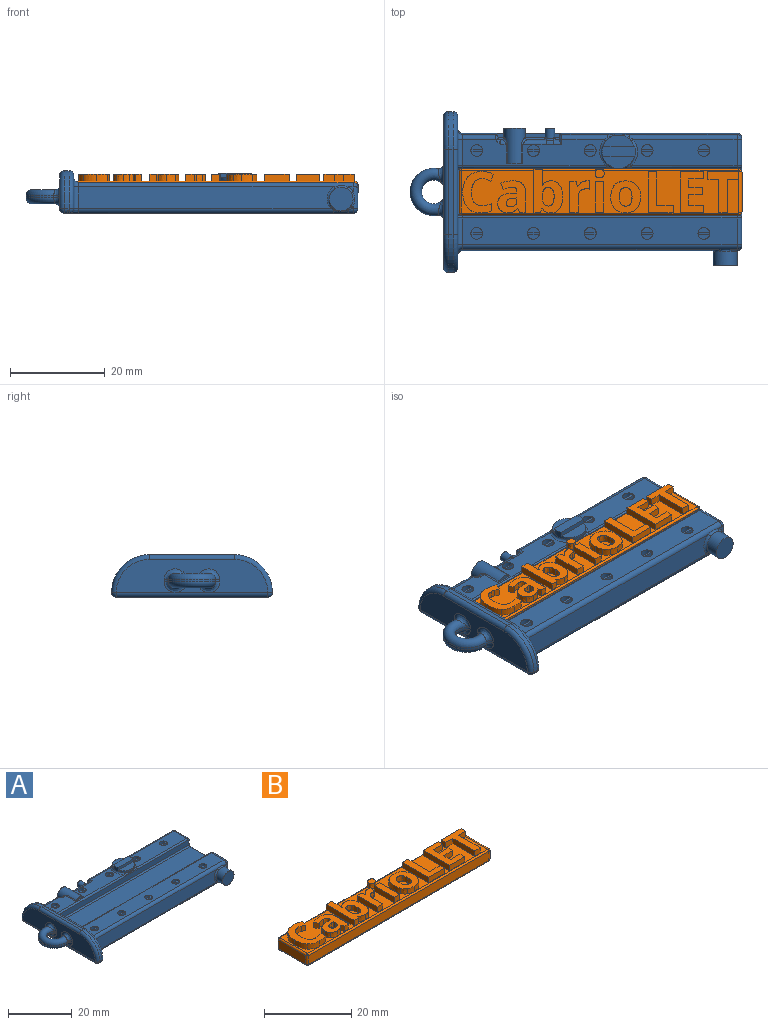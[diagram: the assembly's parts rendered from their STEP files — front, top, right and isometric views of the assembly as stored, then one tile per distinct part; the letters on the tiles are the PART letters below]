
ASSEMBLY  parts=2 mates=1
PART A: 212 faces, bbox 70.7x35.5x9.8 mm
  f0: plane 54.03x4.5mm, normal (0,-1,0.08), area 238.5mm2, adj f1,f2,f3,f4
  f1: cylinder r=1mm len=53.9mm, axis (-1,0,0), area 88.6mm2, adj f0,f5,f6,f7,f8
  f2: bspline ~4.5x1.77mm, area 3.6mm2, adj f0,f6,f9,f10
  f3: cylinder r=1mm len=58mm, axis (1,0,0), area 86.1mm2, adj f0,f9,f11,f12,f13,f14
  f4: cylinder r=1mm len=4.73mm, axis (0,-0.08,-1), area 7.2mm2, adj f0,f7,f14,f15
  f5: bspline ~3.53x1.2mm, area 2.9mm2, adj f1,f8,f16,f17
  f6: bspline ~1.72x1.23mm, area 0.5mm2, adj f1,f2,f10,f17
  f7: bspline ~2.35x2.35mm, area 3.4mm2, adj f1,f4,f8,f18
  f8: plane 61x32mm, normal (0,0,-1), area 1404.4mm2, adj f1,f5,f7,f16,f18,f19,f20,f21
  f9: bspline ~3.78x0.89mm, area 1.8mm2, adj f2,f3,f10,f26
  f10: cylinder r=2.5mm len=5mm, axis (0,1,0), area 43.4mm2, adj f2,f6,f9,f17,f26,f27,f28,f29
  f11: plane 1.03x0.96mm, normal (0,-1,0.08), area 0.4mm2, adj f3,f26,f31
  f12: sphere r=1mm, area 1.5mm2, adj f3,f31,f32
  f13: plane 58x5.57mm, normal (0,0,1), area 298.7mm2, adj f3,f32,f33,f34,f35,f36,f37,f38
  f14: torus R=2mm, axis (1,0,0), area 3.2mm2, adj f3,f4,f15,f39
  f15: plane 32.15x7.15mm, normal (1,0,0), area 68.5mm2, adj f4,f14,f18,f22,f39,f40,f41,f42
  f16: cylinder r=1mm len=1.08mm, axis (-1,0,0), area 1.3mm2, adj f5,f8,f29,f51,f52
  f17: bspline ~3.57x0.73mm, area -0.2mm2, adj f5,f6,f10,f29
  f18: cylinder r=1mm len=2.57mm, axis (0,1,0), area 4mm2, adj f7,f8,f15,f53
  f19: cylinder r=1mm len=1mm, axis (1,0,0), area 1.6mm2, adj f8,f53,f54,f55
  f20: cylinder r=1mm len=32mm, axis (0,-1,0), area 50.3mm2, adj f8,f54,f56,f57
  f21: cylinder r=1mm len=1mm, axis (-1,0,0), area 1.6mm2, adj f8,f56,f58,f59
  f22: cylinder r=1mm len=2.57mm, axis (0,1,0), area 4mm2, adj f8,f15,f23,f59
  f23: bspline ~2.35x2.09mm, area 3.4mm2, adj f8,f22,f24,f46
  f24: cylinder r=1mm len=58mm, axis (1,0,0), area 94.5mm2, adj f8,f23,f60,f61,f62,f63,f64,f65
  f25: cylinder r=1mm len=22.84mm, axis (0,1,0), area 35.9mm2, adj f8,f52,f63,f66
  f26: bspline ~1.28x1.19mm, area 1mm2, adj f9,f10,f11,f27
  f27: bspline ~4.11x1.01mm, area 2.1mm2, adj f10,f26,f30,f31
  f28: plane 5x5mm, normal (0,-1,0), area 19.6mm2, adj f10
  f29: bspline ~1.72x1.23mm, area 0.6mm2, adj f10,f16,f17,f30
  f30: bspline ~0.56x0.54mm, area 0.2mm2, adj f10,f27,f29,f51
  f31: cylinder r=1mm len=4.58mm, axis (0,-0.08,-1), area 6.3mm2, adj f11,f12,f27,f51,f52,f66
  f32: cylinder r=1mm len=5.57mm, axis (0,-1,0), area 8.8mm2, adj f12,f13,f66,f67
  f33: cylinder r=1.25mm len=2.5mm, axis (0,0,1), area 10.5mm2, adj f13,f68,f69,f70,f71,f72
  f34: cylinder r=1.25mm len=2.5mm, axis (0,0,1), area 10.5mm2, adj f13,f73,f74,f75,f76,f77
  f35: cylinder r=1.25mm len=2.5mm, axis (0,0,1), area 10.5mm2, adj f13,f78,f79,f80,f81,f82
  f36: cylinder r=1.25mm len=2.5mm, axis (0,0,1), area 10.5mm2, adj f13,f83,f84,f85,f86,f87
  f37: cylinder r=1.25mm len=2.5mm, axis (0,0,1), area 10.5mm2, adj f13,f88,f89,f90,f91,f92
  f38: cylinder r=0.5mm len=58mm, axis (-1,0,0), area 45.6mm2, adj f13,f40,f50,f67
  f39: cylinder r=1mm len=5.57mm, axis (0,1,0), area 8.8mm2, adj f13,f14,f15,f50
  f40: plane 59.5x2.38mm, normal (0,1,0), area 119.1mm2, adj f15,f38,f50,f67,f93,f94
  f41: cylinder r=0.5mm len=10mm, axis (0,1,0), area 7.5mm2, adj f15,f94,f95,f96
  f42: plane 59.5x2.38mm, normal (0,-1,0), area 119.1mm2, adj f15,f43,f95,f97,f98,f99,f100,f101
  f43: torus R=1.5mm, axis (0,-1,0), area 1mm2, adj f15,f42,f44,f97
  f44: cylinder r=1mm len=5.57mm, axis (0,1,0), area 8.8mm2, adj f15,f43,f45,f103
  f45: torus R=2mm, axis (1,0,0), area 3.2mm2, adj f15,f44,f46,f104
  f46: cylinder r=1mm len=4.73mm, axis (0,0.08,-1), area 7.2mm2, adj f15,f23,f45,f64
  f47: torus R=7mm, axis (1,0,0), area 18.8mm2, adj f15,f48,f58,f59
  f48: cylinder r=1mm len=18mm, axis (0,-1,0), area 28.3mm2, adj f15,f47,f49,f105
  f49: torus R=7mm, axis (1,0,0), area 18.8mm2, adj f15,f48,f53,f55
  f50: torus R=1.5mm, axis (0,-1,0), area 1mm2, adj f15,f38,f39,f40
  f51: plane 0.23x0.17mm, normal (0,-1,0.08), area 0mm2, adj f16,f30,f31
  f52: sphere r=1mm, area 1.6mm2, adj f16,f25,f31
  f53: sphere r=1mm, area 2.1mm2, adj f18,f19,f49
  f54: sphere r=1mm, area 1.6mm2, adj f19,f20,f106
  f55: cylinder r=8mm len=8mm, axis (-1,0,0), area 12.6mm2, adj f19,f49,f105,f106
  f56: sphere r=1mm, area 2.1mm2, adj f20,f21,f107
  f57: plane 32x7mm, normal (-1,0,0), area 203mm2, adj f20,f106,f107,f108
  f58: cylinder r=8mm len=8mm, axis (1,0,0), area 12.6mm2, adj f21,f47,f105,f107
  f59: sphere r=1mm, area 1mm2, adj f21,f22,f47
  f60: plane 14x0.92mm, normal (0,0,1), area 12.1mm2, adj f24,f61,f65,f109,f110,f111
  f61: torus R=0.5mm, axis (1,0,0), area 0mm2, adj f24,f60,f111,f112
  f62: plane 37x5.41mm, normal (0,1,0.08), area 168.6mm2, adj f24,f112,f113,f114,f115,f116,f117,f118
  f63: sphere r=1mm, area 1mm2, adj f24,f25,f114
  f64: plane 7x4.5mm, normal (0,1,0.08), area 31.6mm2, adj f24,f46,f104,f119
  f65: torus R=0.5mm, axis (1,0,0), area 0mm2, adj f24,f60,f109,f119
  f66: plane 22.84x4.5mm, normal (1,0,0), area 74.2mm2, adj f25,f31,f32,f93,f98,f114,f120,f121
  f67: torus R=0.5mm, axis (0,-1,0), area 1mm2, adj f32,f38,f40,f93
  f68: plane 2.5x0.5mm, normal (0,0,1), area 1.2mm2, adj f33,f69,f71
  f69: plane 2.45x1.3mm, normal (0,1,0), area 3.2mm2, adj f33,f68,f70
  f70: plane 2.45x1mm, normal (0,0,1), area 1.8mm2, adj f33,f69
  f71: plane 2.45x1.3mm, normal (0,-1,0), area 3.2mm2, adj f33,f68,f72
  f72: plane 2.45x1mm, normal (0,0,1), area 1.8mm2, adj f33,f71
  f73: plane 2.5x0.5mm, normal (0,0,1), area 1.2mm2, adj f34,f74,f76
  f74: plane 2.45x1.3mm, normal (0,1,0), area 3.2mm2, adj f34,f73,f75
  f75: plane 2.45x1mm, normal (0,0,1), area 1.8mm2, adj f34,f74
  f76: plane 2.45x1.3mm, normal (0,-1,0), area 3.2mm2, adj f34,f73,f77
  f77: plane 2.45x1mm, normal (0,0,1), area 1.8mm2, adj f34,f76
  f78: plane 2.5x0.5mm, normal (0,0,1), area 1.2mm2, adj f35,f79,f81
  f79: plane 2.45x1.3mm, normal (0,1,0), area 3.2mm2, adj f35,f78,f80
  f80: plane 2.45x1mm, normal (0,0,1), area 1.8mm2, adj f35,f79
  f81: plane 2.45x1.3mm, normal (0,-1,0), area 3.2mm2, adj f35,f78,f82
  f82: plane 2.45x1mm, normal (0,0,1), area 1.8mm2, adj f35,f81
  f83: plane 2.5x0.5mm, normal (0,0,1), area 1.2mm2, adj f36,f84,f86
  f84: plane 2.45x1.3mm, normal (0,1,0), area 3.2mm2, adj f36,f83,f85
  f85: plane 2.45x1mm, normal (0,0,1), area 1.8mm2, adj f36,f84
  f86: plane 2.45x1.3mm, normal (0,-1,0), area 3.2mm2, adj f36,f83,f87
  f87: plane 2.45x1mm, normal (0,0,1), area 1.8mm2, adj f36,f86
  f88: plane 2.5x0.5mm, normal (0,0,1), area 1.2mm2, adj f37,f89,f91
  f89: plane 2.45x1.3mm, normal (0,1,0), area 3.2mm2, adj f37,f88,f90
  f90: plane 2.45x1mm, normal (0,0,1), area 1.8mm2, adj f37,f89
  f91: plane 2.45x1.3mm, normal (0,-1,0), area 3.2mm2, adj f37,f88,f92
  f92: plane 2.45x1mm, normal (0,0,1), area 1.8mm2, adj f37,f91
  f93: cylinder r=0.5mm len=1.5mm, axis (0,0,-1), area 1.2mm2, adj f40,f66,f67,f120
  f94: cylinder r=0.5mm len=59.5mm, axis (1,0,0), area 46.5mm2, adj f40,f41,f96,f120
  f95: cylinder r=0.5mm len=59.5mm, axis (-1,0,0), area 46.5mm2, adj f41,f42,f96,f122
  f96: plane 59x9mm, normal (0,0,1), area 531mm2, adj f41,f94,f95,f123
  f97: cylinder r=0.5mm len=30.4mm, axis (1,0,0), area 23.9mm2, adj f42,f43,f102,f103,f124
  f98: cylinder r=0.5mm len=1.5mm, axis (0,0,1), area 1.2mm2, adj f42,f66,f99,f122
  f99: torus R=0.5mm, axis (0,-1,0), area 1mm2, adj f42,f98,f100,f121
  f100: cylinder r=0.5mm len=22.4mm, axis (1,0,0), area 17.6mm2, adj f42,f99,f101,f125,f126
  f101: bspline ~2.65x0.51mm, area 1.1mm2, adj f42,f100,f102,f126
  f102: bspline ~2.65x0.51mm, area 1.1mm2, adj f42,f97,f101,f124
  f103: plane 30.35x5.58mm, normal (0,0,1), area 120.2mm2, adj f44,f97,f104,f113,f127,f128,f129,f130
  f104: cylinder r=1mm len=7.05mm, axis (1,0,0), area 10.5mm2, adj f45,f64,f103,f140,f141
  f105: plane 18x1mm, normal (0,0,1), area 18mm2, adj f48,f55,f58,f108
  f106: torus R=7mm, axis (-1,0,0), area 18.8mm2, adj f54,f55,f57,f108
  f107: torus R=7mm, axis (-1,0,0), area 18.8mm2, adj f56,f57,f58,f108
  f108: cylinder r=1mm len=18mm, axis (0,1,0), area 28.3mm2, adj f57,f105,f106,f107
  f109: plane 4.81x0.45mm, normal (1,0,0), area 1.1mm2, adj f60,f65,f119,f141,f142,f143
  f110: cylinder r=0.5mm len=13mm, axis (-1,0,0), area 10mm2, adj f60,f111,f143,f144
  f111: plane 5x1.05mm, normal (-1,0,0), area 3.6mm2, adj f60,f61,f110,f112,f135,f136,f144,f145
  f112: cylinder r=0.5mm len=4.54mm, axis (0,0.08,-1), area 3.5mm2, adj f61,f62,f111,f145
  f113: cylinder r=1mm len=9.63mm, axis (1,0,0), area 14.2mm2, adj f62,f103,f118,f145,f146
  f114: cylinder r=1mm len=4.58mm, axis (0,0.08,-1), area 7.1mm2, adj f62,f63,f66,f147
  f115: cylinder r=1mm len=22.63mm, axis (1,0,0), area 33.7mm2, adj f62,f116,f125,f147,f148
  f116: bspline ~2.69x1.16mm, area 0.8mm2, adj f62,f115,f149
  f117: bspline ~0.06x0.04mm, area 0mm2, adj f62,f149,f150,f151
  f118: bspline ~2.69x1.16mm, area 0.8mm2, adj f62,f113,f150
  f119: cylinder r=0.5mm len=4.54mm, axis (0,0.08,-1), area 3.5mm2, adj f64,f65,f109,f141
  f120: torus R=1mm, axis (1,0,0), area 0.8mm2, adj f66,f93,f94,f123
  f121: cylinder r=1mm len=5.57mm, axis (0,-1,0), area 8.8mm2, adj f66,f99,f125,f147
  f122: torus R=1mm, axis (1,0,0), area 0.8mm2, adj f66,f95,f98,f123
  f123: cylinder r=0.5mm len=9mm, axis (0,-1,0), area 7.1mm2, adj f66,f96,f120,f122
  f124: bspline ~2.65x0.73mm, area 0.8mm2, adj f97,f102,f134,f152
  f125: plane 22.35x5.57mm, normal (0,0,1), area 109.2mm2, adj f100,f115,f121,f153,f154,f155
  f126: bspline ~2.65x0.73mm, area 0.8mm2, adj f100,f101,f155,f156
  f127: cylinder r=1.25mm len=2.5mm, axis (0,0,1), area 10.5mm2, adj f103,f157,f158,f159,f160,f161
  f128: cylinder r=1mm len=4.92mm, axis (1,0,0), area 6.9mm2, adj f103,f137,f144,f162,f163
  f129: cylinder r=0.5mm len=4mm, axis (0,-1,0), area 1.4mm2, adj f103,f130,f162,f164
  f130: plane 3.55x0.65mm, normal (0,-1,0), area 1.4mm2, adj f103,f129,f131,f164
  f131: cylinder r=0.5mm len=4mm, axis (0,-1,0), area 1.4mm2, adj f103,f130,f164,f165
  f132: cylinder r=1mm len=1.22mm, axis (1,0,0), area 1.2mm2, adj f103,f142,f144,f165
  f133: bspline ~1.37x1mm, area 0.3mm2, adj f103,f140,f142
  f134: torus R=4mm, axis (0,0,1), area 4.5mm2, adj f103,f124,f146,f151,f152
  f135: cylinder r=0.5mm len=1.07mm, axis (0,-1,0), area 0.5mm2, adj f103,f111,f136,f145
  f136: cylinder r=1mm len=1.7mm, axis (1,0,0), area 2mm2, adj f103,f111,f135,f137,f144,f166
  f137: bspline ~2.14x1.15mm, area 1.5mm2, adj f103,f128,f136,f167
  f138: cylinder r=1.25mm len=2.5mm, axis (0,0,1), area 10.5mm2, adj f103,f168,f169,f170,f171,f172
  f139: cylinder r=1.25mm len=2.5mm, axis (0,0,1), area 10.5mm2, adj f103,f173,f174,f175,f176,f177
  f140: bspline ~0.96x0.8mm, area 0.5mm2, adj f104,f133,f141,f142
  f141: torus R=0.5mm, axis (1,0,0), area 0.4mm2, adj f104,f109,f119,f140
  f142: torus R=1.5mm, axis (1,0,0), area 0.7mm2, adj f109,f132,f133,f140,f143
  f143: cylinder r=0.5mm len=4.5mm, axis (0,0,1), area 3.3mm2, adj f109,f110,f142,f144
  f144: plane 12.5x4mm, normal (0,1,0), area 29.6mm2, adj f110,f111,f128,f132,f136,f143,f178,f179
  f145: torus R=0.5mm, axis (1,0,0), area 1mm2, adj f111,f112,f113,f135
  f146: bspline ~1.65x1.1mm, area 0.6mm2, adj f113,f134,f150,f151
  f147: sphere r=1mm, area 1mm2, adj f114,f115,f121
  f148: bspline ~1.83x1.31mm, area 0.6mm2, adj f115,f149,f151,f155
  f149: bspline ~2.44x0.79mm, area 0.7mm2, adj f116,f117,f148,f151
  f150: bspline ~2.4x0.76mm, area 0.7mm2, adj f117,f118,f146,f151
  f151: cylinder r=3.5mm len=7mm, axis (0,0,-1), area 16.7mm2, adj f117,f134,f146,f148,f149,f150,f152,f155
  f152: bspline ~2.38x0.88mm, area 0.9mm2, adj f124,f134,f151,f156
  f153: cylinder r=1.25mm len=2.5mm, axis (0,0,1), area 10.5mm2, adj f125,f185,f186,f187,f188,f189
  f154: cylinder r=1.25mm len=2.5mm, axis (0,0,1), area 10.5mm2, adj f125,f190,f191,f192,f193,f194
  f155: torus R=4mm, axis (0,0,1), area 4.5mm2, adj f125,f126,f148,f151,f156
  f156: bspline ~2.38x0.88mm, area 0.9mm2, adj f126,f151,f152,f155
  f157: plane 2.5x0.5mm, normal (0,0,1), area 1.2mm2, adj f127,f158,f160
  f158: plane 2.45x1.3mm, normal (0,1,0), area 3.2mm2, adj f127,f157,f159
  f159: plane 2.45x1mm, normal (0,0,1), area 1.8mm2, adj f127,f158
  f160: plane 2.45x1.3mm, normal (0,-1,0), area 3.2mm2, adj f127,f157,f161
  f161: plane 2.45x1mm, normal (0,0,1), area 1.8mm2, adj f127,f160
  f162: bspline ~1.57x1.47mm, area 1.1mm2, adj f128,f129,f164,f178
  f163: bspline ~0.97x0.83mm, area 0.4mm2, adj f128,f167,f179,f195
  f164: cylinder r=2.25mm len=7.5mm, axis (0,-1,0), area 47.8mm2, adj f129,f130,f131,f162,f165,f178,f196
  f165: bspline ~1.57x1.47mm, area 1.1mm2, adj f131,f132,f164,f178
  f166: bspline ~1.05x0.78mm, area 0.4mm2, adj f136,f167,f179,f195
  f167: bspline ~1.62x0.46mm, area 0.7mm2, adj f137,f163,f166,f195
  f168: plane 2.45x1.3mm, normal (0,1,0), area 3.2mm2, adj f138,f169,f170
  f169: plane 2.45x1mm, normal (0,0,1), area 1.8mm2, adj f138,f168
  f170: plane 2.5x0.5mm, normal (0,0,1), area 1.2mm2, adj f138,f168,f171
  f171: plane 2.45x1.3mm, normal (0,-1,0), area 3.2mm2, adj f138,f170,f172
  f172: plane 2.45x1mm, normal (0,0,1), area 1.8mm2, adj f138,f171
  f173: plane 2.5x0.5mm, normal (0,0,1), area 1.2mm2, adj f139,f174,f176
  f174: plane 2.45x1.3mm, normal (0,1,0), area 3.2mm2, adj f139,f173,f175
  f175: plane 2.45x1mm, normal (0,0,1), area 1.8mm2, adj f139,f174
  f176: plane 2.45x1.3mm, normal (0,-1,0), area 3.2mm2, adj f139,f173,f177
  f177: plane 2.45x1mm, normal (0,0,1), area 1.8mm2, adj f139,f176
  f178: torus R=2.75mm, axis (0,1,0), area 6.8mm2, adj f144,f162,f164,f165
  f179: torus R=1.5mm, axis (0,1,0), area 3.7mm2, adj f144,f163,f166,f195
  f180: plane 6.71x1mm, normal (0,-1,0), area 6.7mm2, adj f151,f181,f184
  f181: plane 7x2mm, normal (0,0,1), area 13.8mm2, adj f151,f180,f182
  f182: plane 6.71x1mm, normal (0,1,0), area 6.7mm2, adj f151,f181,f183
  f183: plane 6.71x2.5mm, normal (0,0,1), area 12.3mm2, adj f151,f182
  f184: plane 6.71x2.5mm, normal (0,0,1), area 12.3mm2, adj f151,f180
  f185: plane 2.5x0.5mm, normal (0,0,1), area 1.2mm2, adj f153,f186,f188
  f186: plane 2.45x1.3mm, normal (0,1,0), area 3.2mm2, adj f153,f185,f187
  f187: plane 2.45x1mm, normal (0,0,1), area 1.8mm2, adj f153,f186
  f188: plane 2.45x1.3mm, normal (0,-1,0), area 3.2mm2, adj f153,f185,f189
  f189: plane 2.45x1mm, normal (0,0,1), area 1.8mm2, adj f153,f188
  f190: plane 2.5x0.5mm, normal (0,0,1), area 1.2mm2, adj f154,f191,f193
  f191: plane 2.45x1.3mm, normal (0,1,0), area 3.2mm2, adj f154,f190,f192
  f192: plane 2.45x1mm, normal (0,0,1), area 1.8mm2, adj f154,f191
  f193: plane 2.45x1.3mm, normal (0,-1,0), area 3.2mm2, adj f154,f190,f194
  f194: plane 2.45x1mm, normal (0,0,1), area 1.8mm2, adj f154,f193
  f195: cylinder r=1mm len=2.16mm, axis (0,-1,0), area 12.8mm2, adj f163,f166,f167,f179,f197
  f196: plane 4.5x4.5mm, normal (0,1,0), area 15.9mm2, adj f164
  f197: plane 2x2mm, normal (0,1,0), area 3.1mm2, adj f195
  f198: plane 5x4.88mm, normal (1,0,0), area 19.5mm2, adj f199,f200,f201,f202
  f199: bspline ~4.88x2.75mm, area 7.8mm2, adj f198,f200,f202,f203
  f200: cylinder r=1mm len=0.68mm, axis (0,0,-1), area 0.4mm2, adj f198,f199,f201,f204
  f201: bspline ~4.88x2.75mm, area 7.8mm2, adj f198,f200,f202,f205
  f202: cylinder r=1mm len=1.18mm, axis (0,0,-1), area 0.9mm2, adj f198,f199,f201,f206
  f203: torus R=3.75mm, axis (0,0,1), area 56.9mm2, adj f199,f204,f206,f207
  f204: cylinder r=2.5mm len=5mm, axis (0,0,-1), area 6mm2, adj f200,f203,f205,f208
  f205: torus R=3.75mm, axis (0,0,1), area 56.9mm2, adj f201,f204,f206,f209
  f206: cylinder r=5mm len=10mm, axis (0,0,-1), area 8.8mm2, adj f202,f203,f205,f210
  f207: bspline ~4.88x2.75mm, area 7.8mm2, adj f203,f208,f210,f211
  f208: cylinder r=1mm len=0.68mm, axis (0,0,-1), area 0.4mm2, adj f204,f207,f209,f211
  f209: bspline ~4.88x2.75mm, area 7.8mm2, adj f205,f208,f210,f211
  f210: cylinder r=1mm len=1.18mm, axis (0,0,-1), area 0.9mm2, adj f206,f207,f209,f211
  f211: plane 5x4.88mm, normal (1,0,0), area 19.5mm2, adj f207,f208,f209,f210
PART B: 171 faces, bbox 59.7x9.7x4.8 mm
  f0: plane 58.5x8.92mm, normal (0,0,1), area 289.7mm2, adj f6,f7,f8,f9,f10,f11,f12,f13
  f1: plane 58.5x2.66mm, normal (0,1,0), area 146.4mm2, adj f148,f149,f153,f156,f159,f162,f166
  f2: plane 8.9x2.5mm, normal (-1,0,0), area 22.3mm2, adj f151,f157,f158,f162
  f3: plane 58.5x2.5mm, normal (0,-1,0), area 146.2mm2, adj f150,f151,f152,f167
  f4: plane 8.1x1.7mm, normal (1,0,0), area 13.8mm2, adj f163,f166,f167,f170
  f5: plane 58.5x8.9mm, normal (0,0,-1), area 520.6mm2, adj f152,f158,f159,f170
  f6: extruded ~1.58x1.5mm, area 2.7mm2, adj f0,f7,f20,f21
  f7: extruded ~1.5x0.95mm, area 1.5mm2, adj f0,f6,f8,f21
  f8: extruded ~1.5x0.96mm, area 1.6mm2, adj f0,f7,f9,f21
  f9: plane 1.5x1.47mm, normal (0.93,-0.37,0), area 2.4mm2, adj f0,f8,f10,f21
  f10: extruded ~2.49x1.5mm, area 3.9mm2, adj f0,f9,f11,f21
  f11: extruded ~2.12x1.5mm, area 3.3mm2, adj f0,f10,f12,f21
  f12: extruded ~1.53x1.5mm, area 3.2mm2, adj f0,f11,f13,f21
  f13: extruded ~2.33x1.5mm, area 3.6mm2, adj f0,f12,f14,f21
  f14: extruded ~3.24x1.5mm, area 5.2mm2, adj f0,f13,f15,f21
  f15: extruded ~2.84x1.5mm, area 4.7mm2, adj f0,f14,f16,f21
  f16: extruded ~2.34x1.5mm, area 3.6mm2, adj f0,f15,f17,f21
  f17: plane 1.51x1.5mm, normal (1,0,0), area 2.3mm2, adj f0,f16,f18,f21
  f18: extruded ~2.17x1.5mm, area 3.3mm2, adj f0,f17,f19,f21
  f19: extruded ~2.85x2.14mm, area 6.1mm2, adj f0,f18,f20,f21
  f20: extruded ~2.14x1.5mm, area 3.4mm2, adj f0,f6,f19,f21
  f21: plane 8.76x6.49mm, normal (0,0,1), area 25.5mm2, adj f6,f7,f8,f9,f10,f11,f12,f13
  f22: plane 1.5x0.69mm, normal (0.04,-1,0), area 1mm2, adj f23,f46,f47,f48
  f23: plane 1.5x0.54mm, normal (-1,0,0), area 0.8mm2, adj f22,f24,f47,f48
  f24: extruded ~1.5x0.94mm, area 1.6mm2, adj f23,f25,f47,f48
  f25: extruded ~1.5x0.99mm, area 1.6mm2, adj f24,f26,f47,f48
  f26: extruded ~1.5x0.86mm, area 2mm2, adj f25,f27,f47,f48
  f27: extruded ~1.5x0.78mm, area 1.4mm2, adj f26,f46,f47,f48
  f28: plane 1.5x0.89mm, normal (-0.93,-0.36,0), area 1.4mm2, adj f0,f29,f45,f47
  f29: plane 1.5x1.24mm, normal (0,-1,0), area 1.9mm2, adj f0,f28,f30,f47
  f30: plane 4.34x1.5mm, normal (1,0,0), area 6.5mm2, adj f0,f29,f31,f47
  f31: extruded ~1.74x1.5mm, area 2.9mm2, adj f0,f30,f32,f47
  f32: extruded ~2.01x1.5mm, area 3.2mm2, adj f0,f31,f33,f47
  f33: extruded ~2.49x1.5mm, area 3.9mm2, adj f0,f32,f34,f47
  f34: plane 1.5x1.2mm, normal (-0.9,-0.44,0), area 2mm2, adj f0,f33,f35,f47
  f35: extruded ~1.84x1.5mm, area 2.9mm2, adj f0,f34,f36,f47
  f36: extruded ~1.5x1.01mm, area 2.4mm2, adj f0,f35,f37,f47
  f37: plane 1.5x0.29mm, normal (-1,0,0), area 0.4mm2, adj f0,f36,f38,f47
  f38: plane 1.5x1.13mm, normal (-0.03,1,0), area 1.7mm2, adj f0,f37,f39,f47
  f39: extruded ~2.19x1.5mm, area 3.4mm2, adj f0,f38,f40,f47
  f40: extruded ~1.53x1.5mm, area 2.7mm2, adj f0,f39,f41,f47
  f41: extruded ~1.53x1.5mm, area 2.5mm2, adj f0,f40,f42,f47
  f42: extruded ~1.5x1.48mm, area 2.4mm2, adj f0,f41,f43,f47
  f43: extruded ~1.5x1.24mm, area 1.9mm2, adj f0,f42,f44,f47
  f44: extruded ~1.5x0.92mm, area 1.8mm2, adj f0,f43,f45,f47
  f45: plane 1.5x0.05mm, normal (0,-1,0), area 0.1mm2, adj f0,f28,f44,f47
  f46: extruded ~1.5x1.15mm, area 1.8mm2, adj f22,f27,f47,f48
  f47: plane 6.77x5.81mm, normal (0,0,1), area 26mm2, adj f22,f23,f24,f25,f26,f27,f28,f29
  f48: plane 2.22x1.84mm, normal (0,0,1), area 3.3mm2, adj f22,f23,f24,f25,f26,f27,f46
  f49: extruded ~1.5x0.96mm, area 1.6mm2, adj f50,f71,f72,f73
  f50: extruded ~1.5x0.89mm, area 1.6mm2, adj f49,f51,f72,f73
  f51: extruded ~1.5x1.44mm, area 2.2mm2, adj f50,f52,f72,f73
  f52: extruded ~1.5x1.47mm, area 2.3mm2, adj f51,f53,f72,f73
  f53: extruded ~1.5x0.87mm, area 1.6mm2, adj f52,f54,f72,f73
  f54: extruded ~1.5x0.99mm, area 1.7mm2, adj f53,f55,f72,f73
  f55: extruded ~1.5x1.5mm, area 2.3mm2, adj f54,f56,f72,f73
  f56: plane 1.5x0.19mm, normal (1,0,0), area 0.3mm2, adj f55,f71,f72,f73
  f57: extruded ~1.81x1.5mm, area 3.2mm2, adj f0,f58,f70,f72
  f58: extruded ~1.85x1.5mm, area 3.3mm2, adj f0,f57,f59,f72
  f59: plane 1.5x0.07mm, normal (0,1,0), area 0.1mm2, adj f0,f58,f60,f72
  f60: extruded ~1.5x1.29mm, area 1.9mm2, adj f0,f59,f61,f72
  f61: plane 2.11x1.66mm, normal (1,0,0), area 3.2mm2, adj f0,f60,f62,f72,f156
  f62: plane 1.78x1.66mm, normal (0,1,0), area 3mm2, adj f61,f63,f72,f156
  f63: plane 9.07x1.66mm, normal (-1,0,0), area 13.6mm2, adj f0,f62,f64,f72,f156
  f64: plane 1.5x1.36mm, normal (0,-1,0), area 2mm2, adj f0,f63,f65,f72
  f65: plane 1.5x0.72mm, normal (0.92,-0.38,0), area 1.2mm2, adj f0,f64,f66,f72
  f66: plane 1.5x0.12mm, normal (0,-1,0), area 0.2mm2, adj f0,f65,f67,f72
  f67: extruded ~1.8x1.5mm, area 3.1mm2, adj f0,f66,f68,f72
  f68: extruded ~1.83x1.5mm, area 3.2mm2, adj f0,f67,f69,f72
  f69: extruded ~2.5x1.5mm, area 4mm2, adj f0,f68,f70,f72
  f70: extruded ~2.47x1.5mm, area 3.9mm2, adj f0,f57,f69,f72
  f71: extruded ~1.5x1.34mm, area 2.1mm2, adj f49,f56,f72,f73
  f72: plane 9.19x6.09mm, normal (0,0,1), area 32.9mm2, adj f49,f50,f51,f52,f53,f54,f55,f56
  f73: plane 3.89x2.5mm, normal (0,0,1), area 8.1mm2, adj f49,f50,f51,f52,f53,f54,f55,f56
  f74: extruded ~1.5x0.6mm, area 0.9mm2, adj f0,f75,f86,f87
  f75: extruded ~1.5x1.12mm, area 1.8mm2, adj f0,f74,f76,f87
  f76: extruded ~1.5x0.88mm, area 1.8mm2, adj f0,f75,f77,f87
  f77: plane 1.5x0.09mm, normal (0,1,0), area 0.1mm2, adj f0,f76,f78,f87
  f78: plane 1.5x1.1mm, normal (0.97,0.23,0), area 1.7mm2, adj f0,f77,f79,f87
  f79: plane 1.5x1.35mm, normal (0,1,0), area 2mm2, adj f0,f78,f80,f87
  f80: plane 6.52x1.5mm, normal (-1,0,0), area 9.8mm2, adj f0,f79,f81,f87
  f81: plane 1.78x1.5mm, normal (0,-1,0), area 2.7mm2, adj f0,f80,f82,f87
  f82: plane 3.32x1.5mm, normal (1,0,0), area 5mm2, adj f0,f81,f83,f87
  f83: extruded ~1.5x1.22mm, area 2mm2, adj f0,f82,f84,f87
  f84: extruded ~1.5x1.33mm, area 2.1mm2, adj f0,f83,f85,f87
  f85: extruded ~1.5x0.52mm, area 0.8mm2, adj f0,f84,f86,f87
  f86: plane 1.67x1.5mm, normal (1,-0.08,0), area 2.5mm2, adj f0,f74,f85,f87
  f87: plane 6.64x4.24mm, normal (0,0,1), area 15.2mm2, adj f74,f75,f76,f77,f78,f79,f80,f81
  f88: extruded ~1.5x0.97mm, area 2.2mm2, adj f0,f89,f92,f93,f153
  f89: extruded ~1.5x0.97mm, area 2.2mm2, adj f0,f88,f90,f93
  f90: extruded ~1.5x0.73mm, area 1.2mm2, adj f0,f89,f91,f93
  f91: extruded ~1.5x0.64mm, area 1.1mm2, adj f0,f90,f92,f93
  f92: extruded ~1.5x0.97mm, area 2.2mm2, adj f0,f88,f91,f93,f149
  f93: plane 1.94x1.74mm, normal (0,0,1), area 2.8mm2, adj f88,f89,f90,f91,f92
  f94: plane 1.78x1.5mm, normal (0,-1,0), area 2.7mm2, adj f0,f95,f97,f98
  f95: plane 6.52x1.5mm, normal (1,0,0), area 9.8mm2, adj f0,f94,f96,f98
  f96: plane 1.78x1.5mm, normal (0,1,0), area 2.7mm2, adj f0,f95,f97,f98
  f97: plane 6.52x1.5mm, normal (-1,0,0), area 9.8mm2, adj f0,f94,f96,f98
  f98: plane 6.52x1.78mm, normal (0,0,1), area 11.6mm2, adj f94,f95,f96,f97
  f99: extruded ~2.49x1.5mm, area 4mm2, adj f0,f100,f116,f117
  f100: extruded ~1.79x1.5mm, area 2.8mm2, adj f0,f99,f101,f117
  f101: extruded ~1.5x1.17mm, area 2.4mm2, adj f0,f100,f102,f117
  f102: extruded ~1.66x1.5mm, area 2.6mm2, adj f0,f101,f103,f117
  f103: extruded ~2.34x1.5mm, area 3.9mm2, adj f0,f102,f104,f117
  f104: extruded ~2.48x1.5mm, area 4mm2, adj f0,f103,f105,f117
  f105: extruded ~1.8x1.5mm, area 2.8mm2, adj f0,f104,f106,f117
  f106: extruded ~1.5x1.18mm, area 2.5mm2, adj f0,f105,f107,f117
  f107: extruded ~1.66x1.5mm, area 2.6mm2, adj f0,f106,f116,f117
  f108: extruded ~1.5x1.46mm, area 2.3mm2, adj f109,f115,f117,f118
  f109: extruded ~1.5x1.45mm, area 2.3mm2, adj f108,f110,f117,f118
  f110: extruded ~1.5x1.03mm, area 1.8mm2, adj f109,f111,f117,f118
  f111: extruded ~1.5x1.03mm, area 1.8mm2, adj f110,f112,f117,f118
  f112: extruded ~1.5x1.45mm, area 2.3mm2, adj f111,f113,f117,f118
  f113: extruded ~1.5x1.47mm, area 2.3mm2, adj f112,f114,f117,f118
  f114: extruded ~1.5x1.02mm, area 1.8mm2, adj f113,f115,f117,f118
  f115: extruded ~1.5x1.03mm, area 1.8mm2, adj f108,f114,f117,f118
  f116: extruded ~2.34x1.5mm, area 3.9mm2, adj f0,f99,f107,f117
  f117: plane 6.76x6.32mm, normal (0,0,1), area 26mm2, adj f99,f100,f101,f102,f103,f104,f105,f106
  f118: plane 3.89x2.69mm, normal (0,0,1), area 8.8mm2, adj f108,f109,f110,f111,f112,f113,f114,f115
  f119: plane 8.52x1.5mm, normal (-1,0,0), area 12.8mm2, adj f0,f120,f124,f125
  f120: plane 5.26x1.5mm, normal (0,-1,0), area 7.9mm2, adj f0,f119,f121,f125
  f121: plane 1.5x1.49mm, normal (1,0,0), area 2.2mm2, adj f0,f120,f122,f125
  f122: plane 3.46x1.5mm, normal (0,1,0), area 5.2mm2, adj f0,f121,f123,f125
  f123: plane 7.03x1.5mm, normal (1,0,0), area 10.5mm2, adj f0,f122,f124,f125
  f124: plane 1.81x1.5mm, normal (0,1,0), area 2.7mm2, adj f0,f119,f123,f125
  f125: plane 8.52x5.26mm, normal (0,0,1), area 20.6mm2, adj f119,f120,f121,f122,f123,f124
  f126: plane 4.91x1.5mm, normal (0,-1,0), area 7.4mm2, adj f0,f127,f137,f138
  f127: plane 1.5x1.49mm, normal (1,0,0), area 2.2mm2, adj f0,f126,f128,f138
  f128: plane 3.1x1.5mm, normal (0,1,0), area 4.6mm2, adj f0,f127,f129,f138
  f129: plane 2.2x1.5mm, normal (1,0,0), area 3.3mm2, adj f0,f128,f130,f138
  f130: plane 2.89x1.5mm, normal (0,-1,0), area 4.3mm2, adj f0,f129,f131,f138
  f131: plane 1.5x1.48mm, normal (1,0,0), area 2.2mm2, adj f0,f130,f132,f138
  f132: plane 2.89x1.5mm, normal (0,1,0), area 4.3mm2, adj f0,f131,f133,f138
  f133: plane 1.87x1.5mm, normal (1,0,0), area 2.8mm2, adj f0,f132,f134,f138
  f134: plane 3.1x1.5mm, normal (0,-1,0), area 4.6mm2, adj f0,f133,f135,f138
  f135: plane 1.5x1.48mm, normal (1,0,0), area 2.2mm2, adj f0,f134,f136,f138
  f136: plane 4.91x1.5mm, normal (0,1,0), area 7.4mm2, adj f0,f135,f137,f138
  f137: plane 8.52x1.5mm, normal (-1,0,0), area 12.8mm2, adj f0,f126,f136,f138
  f138: plane 8.52x4.91mm, normal (0,0,1), area 28.9mm2, adj f126,f127,f128,f129,f130,f131,f132,f133
  f139: plane 1.81x1.5mm, normal (0,-1,0), area 2.7mm2, adj f0,f140,f146,f147
  f140: plane 7.02x1.5mm, normal (1,0,0), area 10.5mm2, adj f0,f139,f141,f147
  f141: plane 2.31x1.5mm, normal (0,-1,0), area 3.5mm2, adj f0,f140,f142,f147,f163
  f142: plane 1.5x1.5mm, normal (1,0,0), area 2.3mm2, adj f141,f143,f147,f163
  f143: plane 6.43x1.5mm, normal (0,1,0), area 9.7mm2, adj f0,f142,f144,f147,f163
  f144: plane 1.5x1.5mm, normal (-1,0,0), area 2.3mm2, adj f0,f143,f145,f147
  f145: plane 2.31x1.5mm, normal (0,-1,0), area 3.5mm2, adj f0,f144,f146,f147
  f146: plane 7.02x1.5mm, normal (-1,0,0), area 10.5mm2, adj f0,f139,f145,f147
  f147: plane 8.52x6.43mm, normal (0,0,1), area 22.4mm2, adj f139,f140,f141,f142,f143,f144,f145,f146
  f148: cylinder r=0.4mm len=28.47mm, axis (1,0,0), area 17.9mm2, adj f0,f1,f149,f164
  f149: bspline ~0.82x0.4mm, area 0.3mm2, adj f1,f92,f148,f153
  f150: cylinder r=0.4mm len=58.5mm, axis (-1,0,0), area 36.8mm2, adj f0,f3,f154,f165
  f151: cylinder r=0.4mm len=2.5mm, axis (0,0,-1), area 1.6mm2, adj f2,f3,f154,f155
  f152: cylinder r=0.4mm len=58.5mm, axis (1,0,0), area 36.8mm2, adj f3,f5,f155,f169
  f153: bspline ~0.82x0.4mm, area 0.3mm2, adj f1,f88,f149,f156
  f154: sphere r=0.4mm, area 0.3mm2, adj f150,f151,f157
  f155: sphere r=0.4mm, area 0.3mm2, adj f151,f152,f158
  f156: cylinder r=0.4mm len=28.39mm, axis (1,0,0), area 17.2mm2, adj f0,f1,f61,f62,f63,f153,f160
  f157: cylinder r=0.4mm len=8.9mm, axis (0,1,0), area 5.6mm2, adj f0,f2,f154,f160
  f158: cylinder r=0.4mm len=8.9mm, axis (0,-1,0), area 5.6mm2, adj f2,f5,f155,f161
  f159: cylinder r=0.4mm len=58.5mm, axis (-1,0,0), area 36.8mm2, adj f1,f5,f161,f168
  f160: sphere r=0.4mm, area 0.3mm2, adj f156,f157,f162
  f161: sphere r=0.4mm, area 0.3mm2, adj f158,f159,f162
  f162: cylinder r=0.4mm len=2.5mm, axis (0,0,1), area 1.6mm2, adj f1,f2,f160,f161
  f163: cylinder r=0.8mm len=8.9mm, axis (0,-1,0), area 10.8mm2, adj f0,f4,f141,f142,f143,f164,f165
  f164: bspline ~0.84x0.8mm, area 0.5mm2, adj f148,f163,f166
  f165: bspline ~0.96x0.8mm, area 0.5mm2, adj f150,f163,f167
  f166: cylinder r=0.8mm len=2.5mm, axis (0,0,-1), area 2.6mm2, adj f1,f4,f164,f168
  f167: cylinder r=0.8mm len=2.5mm, axis (0,0,1), area 2.6mm2, adj f3,f4,f165,f169
  f168: bspline ~0.96x0.8mm, area 0.5mm2, adj f159,f166,f170
  f169: bspline ~0.84x0.8mm, area 0.5mm2, adj f152,f167,f170
  f170: cylinder r=0.8mm len=8.9mm, axis (0,1,0), area 10.7mm2, adj f4,f5,f168,f169
PLACE A t=(-6.06,-15.11,-12.54)mm
PLACE B t=(-17.58,-6.68,-9.04)mm
MATE fastened A.f96 <-> B.f5  axis (0,0,1) through (22.07,8.17,-9.04)mm
